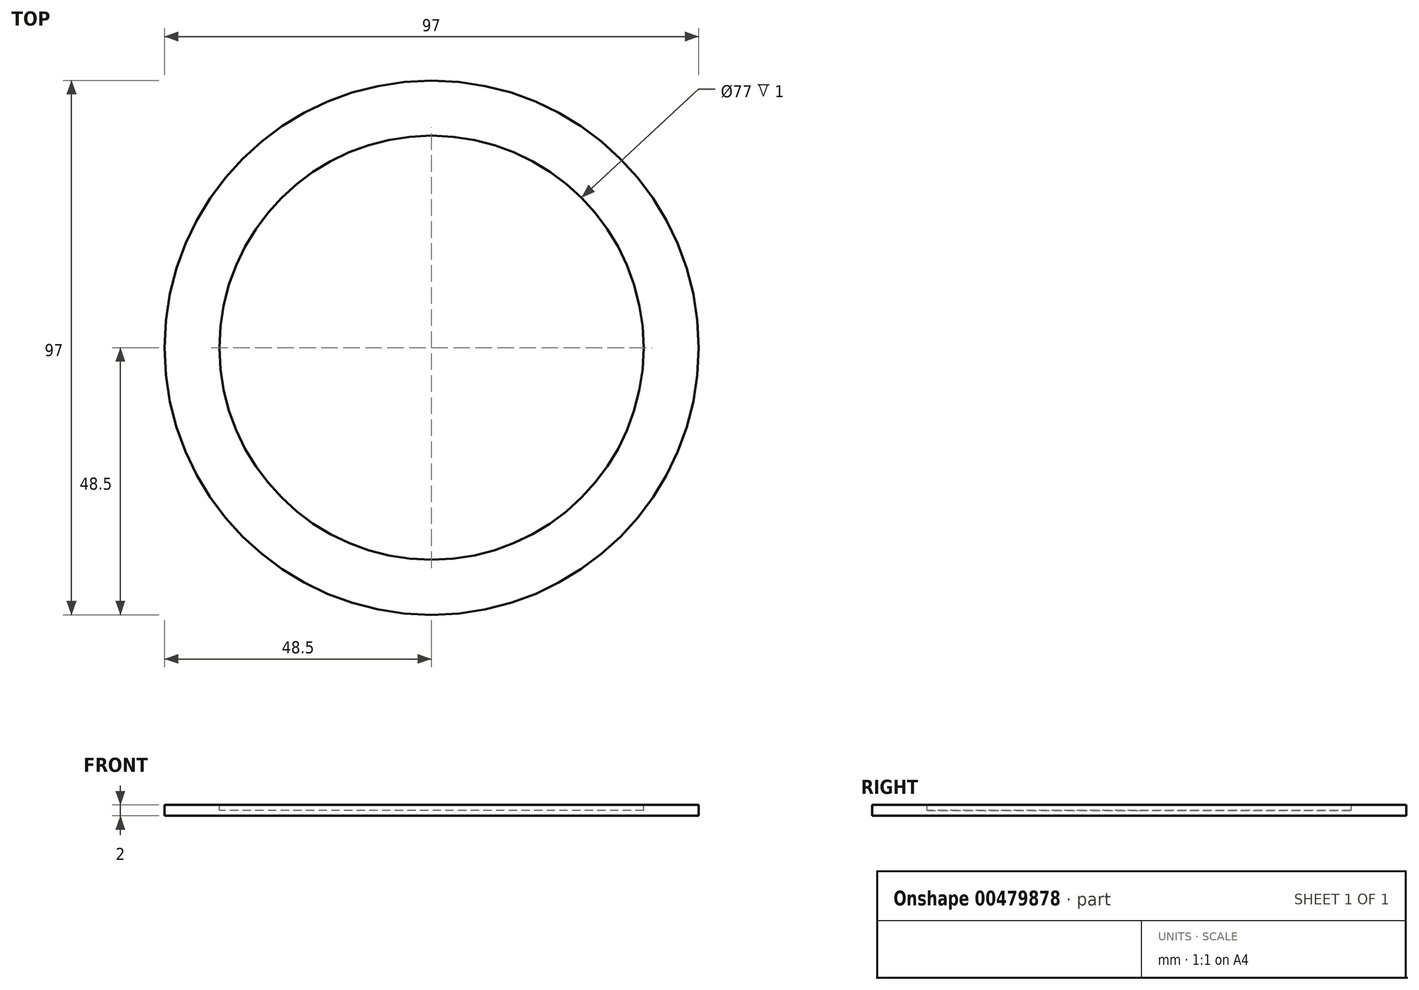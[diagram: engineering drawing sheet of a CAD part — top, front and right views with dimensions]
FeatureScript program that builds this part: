
annotation { "Feature Type Name" : "Feature", "Feature Type Description" : "" }
export const myFeature = defineFeature(function(context is Context, id is Id, definition is map)
    precondition{}
    {
        {
            var Q0;
            Q0=qCreatedBy(makeId("Top.planeOp"),FACE);
            var sketch = newSketch(context, id + "F0", { "sketchPlane" : qUnion([Q0])});
            skCircle(sketch, "E0", {"center": v(0, 0) * mm, "radius": 48.5 * mm});
            skSolve(sketch);
        }
        {
            var Q0;
            Q0=makeQuery(id+"F0.imprint","IMPRINT",FACE,{"disambiguationData":[TD([[makeQuery(id+"F0.imprint","IMPRINT",EDGE,{"derivedFrom":sQuery(id+"F0.wireOp",EDGE,"E0")}),1.0]])]});
            extrude(context, id + "F1", {"entities" : qUnion([Q0]), "depth" : 2 * mm});
        }
        {
            var Q0;
            Q0=makeQuery(id+"F1.opExtrude","CAP_FACE",FACE,{"disambiguationData":[OSD([sQuery(id+"F0.wireOp",EDGE,"E0")])],"isStart":false});
            var sketch = newSketch(context, id + "F2", { "sketchPlane" : qUnion([Q0])});
            skCircle(sketch, "E1", {"center": v(0, 0) * mm, "radius": 37.5 * mm});
            skCircle(sketch, "E2", {"center": v(0, 1.04) * mm, "radius": 27.96 * mm});
            skSolve(sketch);
        }
        {
            var Q0;
            Q0=makeQuery(id+"FzYNrNnkmtAAcH3_1.boolean.opBoolean","SPLIT",FACE,{"disambiguationData":[TD([makeQuery(id+"FzYNrNnkmtAAcH3_1.opExtrude","SWEPT_FACE",FACE,{"disambiguationData":[OSD([sQuery(id+"F2.wireOp",EDGE,"E2")])]})])],"derivedFrom":makeQuery(id+"F1.opExtrude","CAP_FACE",FACE,{"disambiguationData":[OSD([sQuery(id+"F0.wireOp",EDGE,"E0")])],"isStart":false})});
            var sketch = newSketch(context, id + "F3", { "sketchPlane" : qUnion([Q0])});
            skText(sketch, "E3", { "text": "SGS", "fontName": "RobotoSlab-Regular.ttf"});
            skText(sketch, "E4", { "text": "7", "fontName": "RobotoSlab-Regular.ttf"});
            const initialGuessF3  = {"E3": [-0.01654, 0.005, 1, 0, 0.01247], "E4": [-0.0065, -0.02117, 1, 0, 0.01617]};
            skSetInitialGuess(sketch, initialGuessF3);
            skSolve(sketch);
        }
        {
            var Q0;
            Q0=makeQuery(id+"F3.imprint","IMPRINT",FACE,{"disambiguationData":[TD([[makeQuery(id+"F3.imprint","IMPRINT",EDGE,{"derivedFrom":sQuery(id+"F3.wireOp",EDGE,"E3.sketch_text.stroke-0")}),1.0]])]});
            var sketch = newSketch(context, id + "F4", { "sketchPlane" : qUnion([Q0])});
            skCircle(sketch, "E5", {"center": v(0, 0) * mm, "radius": 38.5 * mm});
            skSolve(sketch);
        }
        {
            var Q0;
            Q0 = qSketchRegion(id + "F4", true);
            extrude(context, id + "F5", {"entities" : qUnion([Q0]), "operationType" : NewBodyOperationType.REMOVE, "oppositeDirection" : true, "depth" : 1 * mm});
        }
    });
